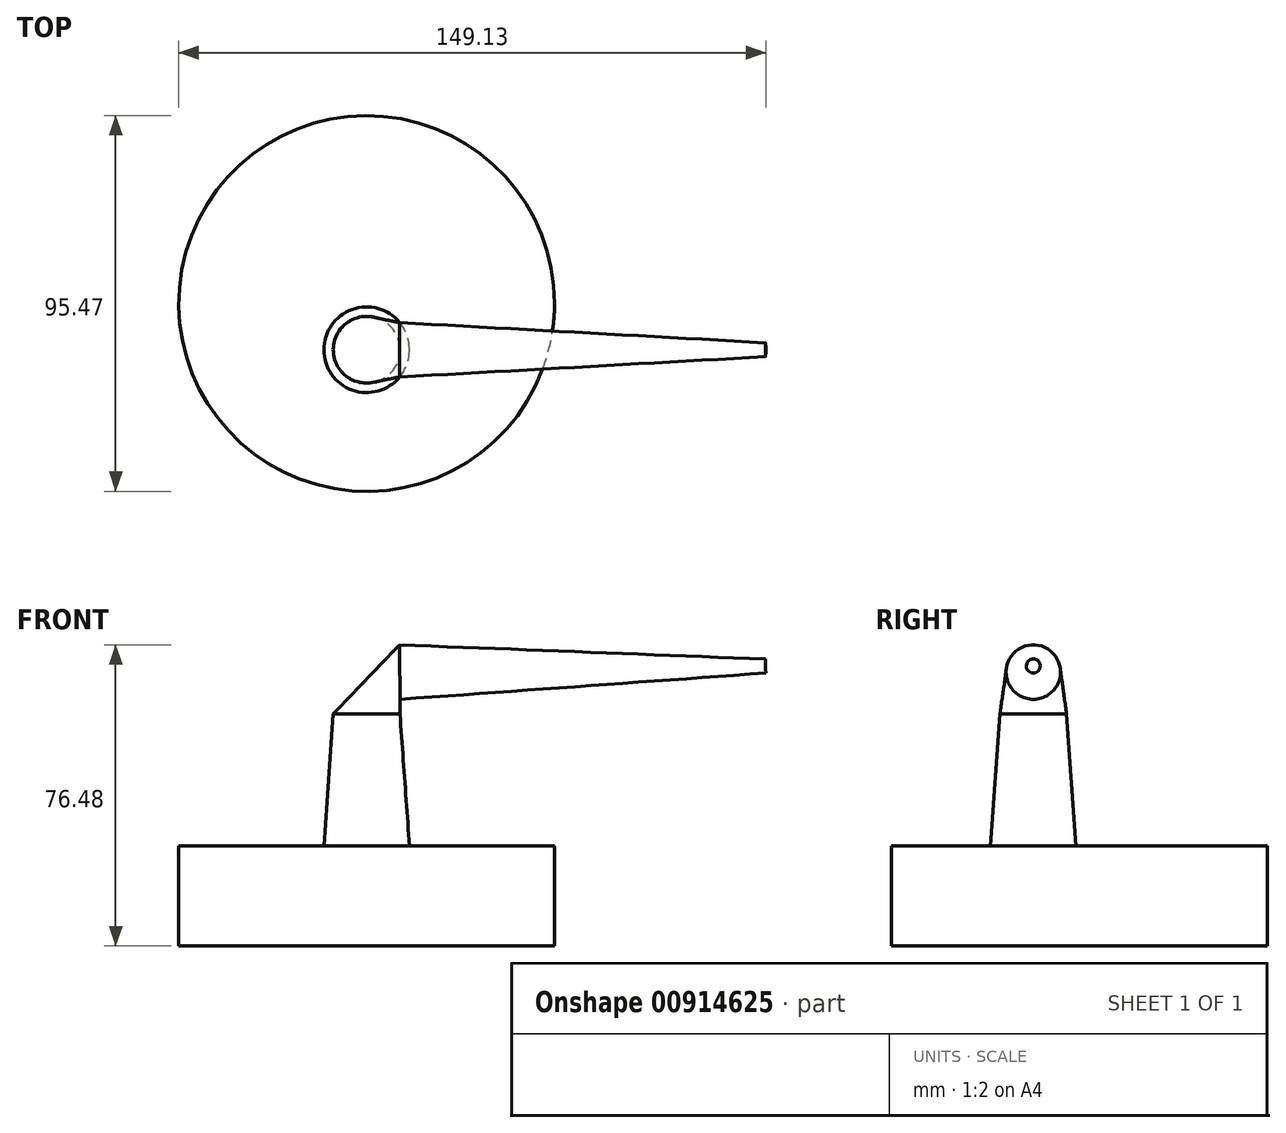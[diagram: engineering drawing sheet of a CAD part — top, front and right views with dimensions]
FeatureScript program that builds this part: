
annotation { "Feature Type Name" : "Feature", "Feature Type Description" : "" }
export const myFeature = defineFeature(function(context is Context, id is Id, definition is map)
    precondition{}
    {
        {
            var Q0;
            Q0=qCreatedBy(makeId("Top.planeOp"),FACE);
            var sketch = newSketch(context, id + "F0", { "sketchPlane" : qUnion([Q0])});
            skCircle(sketch, "E0", {"center": v(0, 0) * mm, "radius": 12.7 * mm});
            skSolve(sketch);
        }
        {
            var Q0;
            Q0=makeQuery(id+"F0.imprint","IMPRINT",FACE,{"disambiguationData":[TD([[makeQuery(id+"F0.imprint","IMPRINT",EDGE,{"derivedFrom":sQuery(id+"F0.wireOp",EDGE,"E0")}),1.0]])]});
            cPlane(context, id + "F1", {"entities" : qUnion([Q0]), "cplaneType" : CPlaneType.OFFSET, "offset" : 58.93 * mm, "width" : 152.4 * mm, "height" : 152.4 * mm});
        }
        {
            var Q0;
            Q0=qCreatedBy(id+"F1.planeOp",FACE);
            var sketch = newSketch(context, id + "F2", { "sketchPlane" : qUnion([Q0])});
            skCircle(sketch, "E1", {"center": v(0, 0) * mm, "radius": 8.47 * mm});
            skSolve(sketch);
        }
        {
            var Q0;
            Q0=makeQuery(id+"F0.imprint","IMPRINT",FACE,{"disambiguationData":[TD([[makeQuery(id+"F0.imprint","IMPRINT",EDGE,{"derivedFrom":sQuery(id+"F0.wireOp",EDGE,"E0")}),1.0]])]});
            var Q1;
            Q1=makeQuery(id+"F2.imprint","IMPRINT",FACE,{"disambiguationData":[TD([[makeQuery(id+"F2.imprint","IMPRINT",EDGE,{"derivedFrom":sQuery(id+"F2.wireOp",EDGE,"E1")}),1.0]])]});
            loft(context, id + "F3", {"sheetProfilesArray" : [{ "sheetProfileEntities" : qUnion([Q0]) }, { "sheetProfileEntities" : qUnion([Q1]) }]});
        }
        {
            var Q0;
            Q0=qCreatedBy(makeId("Front.planeOp"),FACE);
            var sketch = newSketch(context, id + "F4", { "sketchPlane" : qUnion([Q0])});
            skFitSpline(sketch, "E2", {"points": [v(0, 61.23) * mm, v(0, 67.82) * mm, v(8.41, 69.54) * mm], "startDerivative": vector(-3.69, 16.67) * mm, "endDerivative": vector(20, 0.32) * mm});
            skSolve(sketch);
        }
        {
            var Q0;
            Q0=sQuery(id+"F4.wireOp",VERTEX,"E2.end");
            var Q1;
            Q1=sQuery(id+"F4.wireOp",EDGE,"E2");
            cPlane(context, id + "F5", {"entities" : qUnion([Q0, Q1]), "cplaneType" : CPlaneType.CURVE_POINT, "offset" : 25.4 * mm, "width" : 152.4 * mm, "height" : 152.4 * mm});
        }
        {
            var Q0;
            Q0=qCreatedBy(id+"F5.planeOp",FACE);
            var sketch = newSketch(context, id + "F6", { "sketchPlane" : qUnion([Q0])});
            skCircle(sketch, "E3", {"center": v(0, 69.42) * mm, "radius": 6.91 * mm});
            skSolve(sketch);
        }
        {
            var Q0;
            Q0=makeQuery(id+"F3.opLoft","CAP_FACE",FACE,{"disambiguationData":[OSD([makeQuery(id+"F2.imprint","IMPRINT",FACE,{"disambiguationData":[TD([[makeQuery(id+"F2.imprint","IMPRINT",EDGE,{"derivedFrom":sQuery(id+"F2.wireOp",EDGE,"E1")}),1.0]])]})])],"isStart":true});
            var Q1;
            Q1=makeQuery(id+"F6.imprint","IMPRINT",FACE,{"disambiguationData":[TD([[makeQuery(id+"F6.imprint","IMPRINT",EDGE,{"derivedFrom":sQuery(id+"F6.wireOp",EDGE,"E3")}),1.0]])]});
            loft(context, id + "F7", {"sheetProfilesArray" : [{ "sheetProfileEntities" : qUnion([Q0]) }, { "sheetProfileEntities" : qUnion([Q1]) }]});
        }
        {
            var Q0;
            Q0=makeQuery(id+"F7.opLoft","CAP_FACE",FACE,{"disambiguationData":[OSD([makeQuery(id+"F6.imprint","IMPRINT",FACE,{"disambiguationData":[TD([[makeQuery(id+"F6.imprint","IMPRINT",EDGE,{"derivedFrom":sQuery(id+"F6.wireOp",EDGE,"E3")}),1.0]])]})])],"isStart":true});
            cPlane(context, id + "F8", {"entities" : qUnion([Q0]), "cplaneType" : CPlaneType.OFFSET, "offset" : 92.96 * mm, "width" : 152.4 * mm, "height" : 152.4 * mm});
        }
        {
            var Q0;
            Q0=qCreatedBy(id+"F8.planeOp",FACE);
            var sketch = newSketch(context, id + "F9", { "sketchPlane" : qUnion([Q0])});
            skCircle(sketch, "E4", {"center": v(0, 69.46) * mm, "radius": 1.77 * mm});
            skSolve(sketch);
        }
        {
            var Q1;
            Q1=makeQuery(id+"F7.opLoft","CAP_FACE",FACE,{"disambiguationData":[OSD([makeQuery(id+"F6.imprint","IMPRINT",FACE,{"disambiguationData":[TD([[makeQuery(id+"F6.imprint","IMPRINT",EDGE,{"derivedFrom":sQuery(id+"F6.wireOp",EDGE,"E3")}),1.0]])]})])],"isStart":true});
            var Q2;
            Q2=makeQuery(id+"F9.imprint","IMPRINT",FACE,{"disambiguationData":[TD([[makeQuery(id+"F9.imprint","IMPRINT",EDGE,{"derivedFrom":sQuery(id+"F9.wireOp",EDGE,"E4")}),1.0]])]});
            loft(context, id + "F10", {"operationType" : NewBodyOperationType.ADD, "sheetProfilesArray" : [{ "sheetProfileEntities" : qUnion([Q1]) }, { "sheetProfileEntities" : qUnion([Q2]) }]});
        }
        {
            var Q0;
            Q0=qCreatedBy(makeId("Top.planeOp"),FACE);
            var sketch = newSketch(context, id + "F11", { "sketchPlane" : qUnion([Q0])});
            skCircle(sketch, "E5", {"center": v(0, 11.76) * mm, "radius": 47.74 * mm});
            skSolve(sketch);
        }
        {
            var Q0;
            Q0=makeQuery(id+"F11.imprint","IMPRINT",FACE,{"disambiguationData":[TD([[makeQuery(id+"F11.imprint","IMPRINT",EDGE,{"derivedFrom":sQuery(id+"F11.wireOp",EDGE,"E5")}),1.0]])]});
            extrude(context, id + "F12", {"entities" : qUnion([Q0]), "operationType" : NewBodyOperationType.ADD, "depth" : 25.4 * mm, "offsetDistance" : 25.4 * mm});
        }
    });
